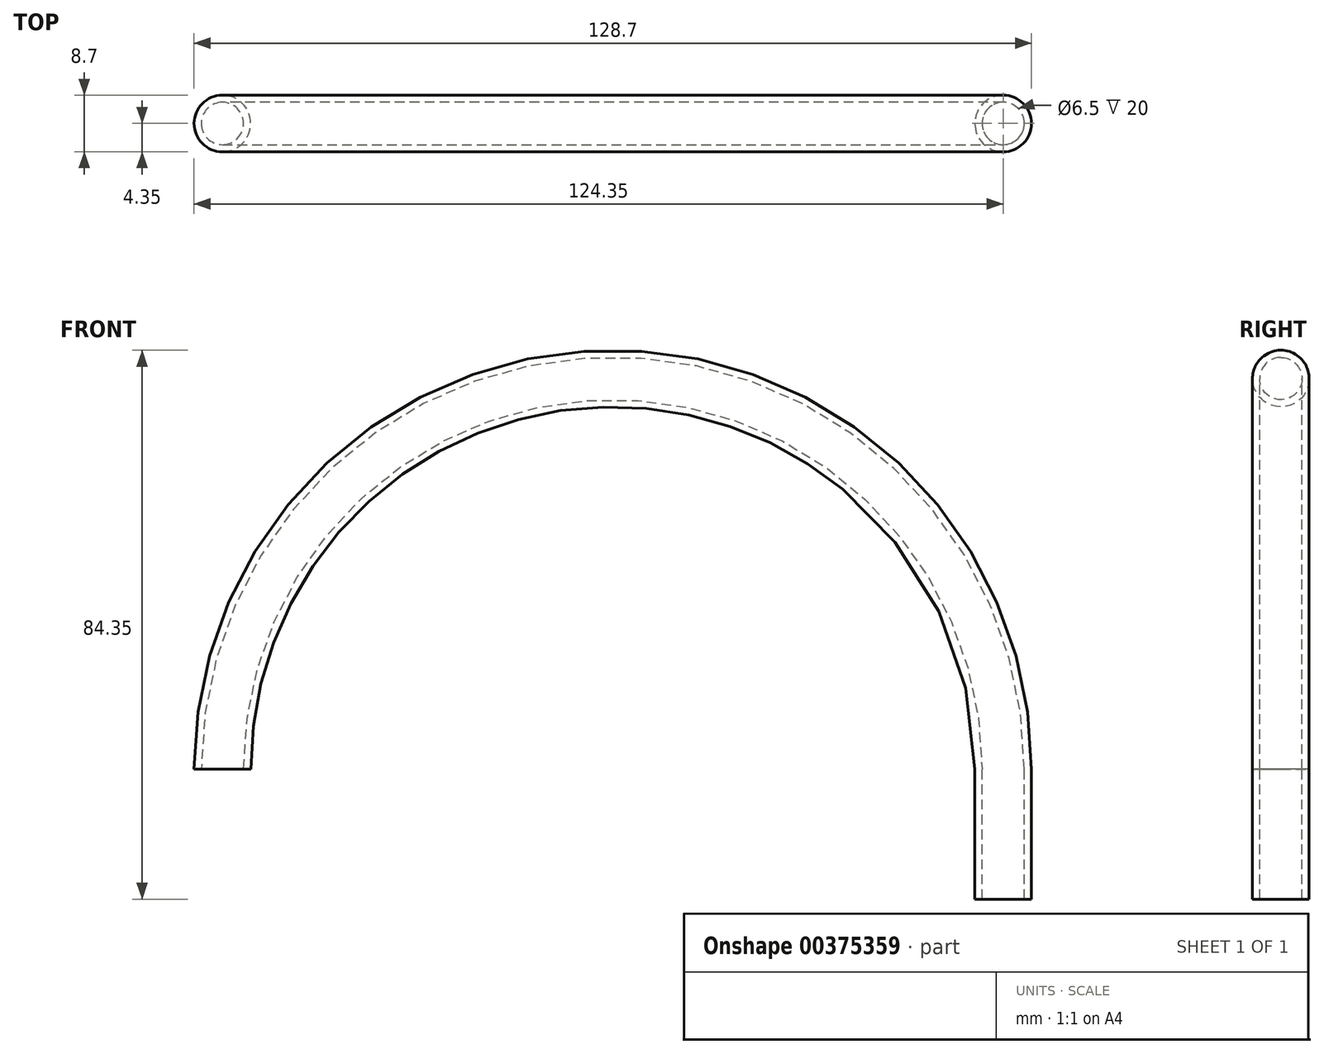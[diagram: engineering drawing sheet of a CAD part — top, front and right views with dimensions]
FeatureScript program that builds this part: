
annotation { "Feature Type Name" : "Feature", "Feature Type Description" : "" }
export const myFeature = defineFeature(function(context is Context, id is Id, definition is map)
    precondition{}
    {
        {
            var Q0;
            Q0=qCreatedBy(makeId("Top.planeOp"),FACE);
            var sketch = newSketch(context, id + "F0", { "sketchPlane" : qUnion([Q0])});
            skCircle(sketch, "E0", {"center": v(0, 0) * mm, "radius": 4.35 * mm});
            skSolve(sketch);
        }
        {
            var Q0;
            Q0=makeQuery(id+"F0.imprint","IMPRINT",FACE,{"disambiguationData":[TD([[makeQuery(id+"F0.imprint","IMPRINT",EDGE,{"derivedFrom":sQuery(id+"F0.wireOp",EDGE,"E0")}),1.0]])]});
            extrude(context, id + "F1", {"entities" : qUnion([Q0]), "depth" : 20 * mm});
        }
        {
            var Q0;
            Q0=makeQuery(id+"F1.opExtrude","CAP_FACE",FACE,{"disambiguationData":[OSD([sQuery(id+"F0.wireOp",EDGE,"E0")])],"isStart":false});
            var sketch = newSketch(context, id + "F2", { "sketchPlane" : qUnion([Q0])});
            skCircle(sketch, "E1", {"center": v(0, 0) * mm, "radius": 3.25 * mm});
            skSolve(sketch);
        }
        {
            var Q0;
            Q0=makeQuery(id+"F2.imprint","IMPRINT",FACE,{"disambiguationData":[TD([[makeQuery(id+"F2.imprint","IMPRINT",EDGE,{"derivedFrom":sQuery(id+"F2.wireOp",EDGE,"E1")}),1.0]])]});
            extrude(context, id + "F3", {"entities" : qUnion([Q0]), "operationType" : NewBodyOperationType.REMOVE, "oppositeDirection" : true, "depth" : 25 * mm});
        }
        {
            var Q0;
            Q0=qCreatedBy(makeId("Front.planeOp"),FACE);
            var sketch = newSketch(context, id + "F4", { "sketchPlane" : qUnion([Q0])});
            skLineSegment(sketch, "E2", {"start": v(0, 28.74) * mm, "end": v(0, -19.75) * mm, "construction": true});
            skLineSegment(sketch, "E3", {"start": v(-61.15, 20) * mm, "end": v(28.75, 20) * mm, "construction": true});
            skLineSegment(sketch, "E4.0", {"start": v(-4.35, 20) * mm, "end": v(4.35, 20) * mm});
            skArc(sketch, "E5", {"start": v(0, 20) * mm, "mid": v(-60, 80) * mm, "end": v(-120, 20) * mm});
            skPoint(sketch, "E5.endSnap0", {"position": v(0, 20) * mm});
            skSolve(sketch);
        }
        {
            var Q0;
            Q0=makeQuery(id+"F1.opExtrude","CAP_FACE",FACE,{"disambiguationData":[OSD([sQuery(id+"F0.wireOp",EDGE,"E0")])],"isStart":false});
            var Q1;
            Q1=sQuery(id+"F4.wireOp",EDGE,"E5");
            sweep(context, id + "F5", {"operationType" : NewBodyOperationType.ADD, "profiles" : qUnion([Q0]), "path" : qUnion([Q1])});
        }
    });
